# Revit family: Toilet_Seat-Elongated_Closed_Front-KOHLER-C3-K-8298
name_source: partatom
category: Specialty Equipment
revit_build: Autodesk Revit 2015 (Build: 20140606_1530(x64)
units: mm (PartAtom-declared; Revit-internal decimal feet)

## types (3) — shared parameters
ADA Compliant = No
Apparent Load = 1800 VA
Assembly Code = C1030200
CW Connection = Yes
Cold Water Inlet = Cold Water Inlet
Date Modified = 11/20/2018
Default Elevation = 0"
Description = Elongated toilet seat
Electrical Connector = Yes
Electrical Note = One dedicated circuit required, protected with Class A Ground-Fault Circuit-Interrupter (GFCI) or Residual Current Device (RCD)
Height = 5 1/8"
Length = 20 5/8"
Manufacturer = KOHLER Co.
MasterFormat 1995 = 10820
MasterFormat 2004 = 10.28.13
Material = Polypropylene Plastic
Product Documentation Link = http://www.us.kohler.com
Product Page URL = http://www.us.kohler.com
URL = https://www.us.kohler.com
Voltage = 120 V

## per-type parameters (varying)
| type | Finish | Model | Product Name | Side Panel | Type | Width | Without Side Panel |
| Without Side Control Panel, 0-White | Kohler-Plastic-0-White | K-8298-CR-0 | C3-455 | No | 3 | 15 1/2" | Yes |
| With Side Control Panel, 0-White | Kohler-Plastic-0-White | K-8298-0 | C3-155 | Yes | 1 | 17 5/8" | No |
| With Side Control Panel, 96-Biscuit | Kohler-Plastic-96-Biscuit | K-8298-96 | C3-155 | Yes | 2 | 17 5/8" | No |

## geometry (parser evidence)
native form markers: Sweep x6
no freeform markers — native parametric forms only
